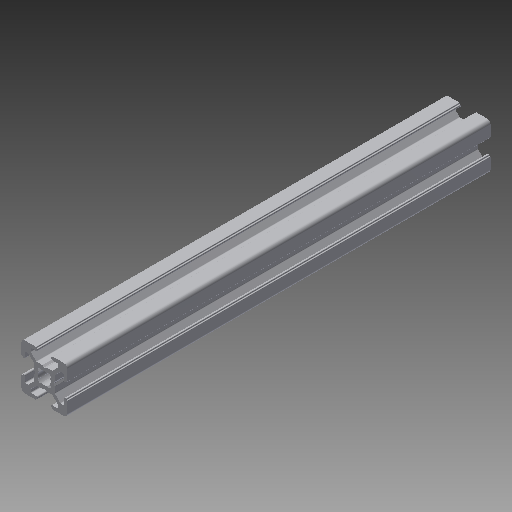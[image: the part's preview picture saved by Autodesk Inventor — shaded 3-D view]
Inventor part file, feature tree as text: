
AUTODESK INVENTOR PART (.ipt)
format: ipt  version: 2017 (Build 210142000, 142)  size: 314,880 bytes
history: native  units: in
note: dims shown in document units (in); Inventor stores cm internally (conversion verified against a paired STEP export)
features: other x3, extrude x1, sketch x1
ambient origin geometry x8: Origin, YZ Plane, XZ Plane, XY Plane, X Axis, Y Axis, Z Axis, Center Point
bodies: Solid1 (feature_tree)
feature tree (5):
  other  "Blocks"
  extrude  "Extrusion1"  [1 undecoded]
  sketch  "Sketch1"  dims[d1=0.0in]
  other  "20x20"
  other  "20x20:1"
note: 1 required parameter value undecoded (feature->parameter linkage not recoverable at this tier; creation-order binding heuristic only, values carry confidence <= 0.55)
